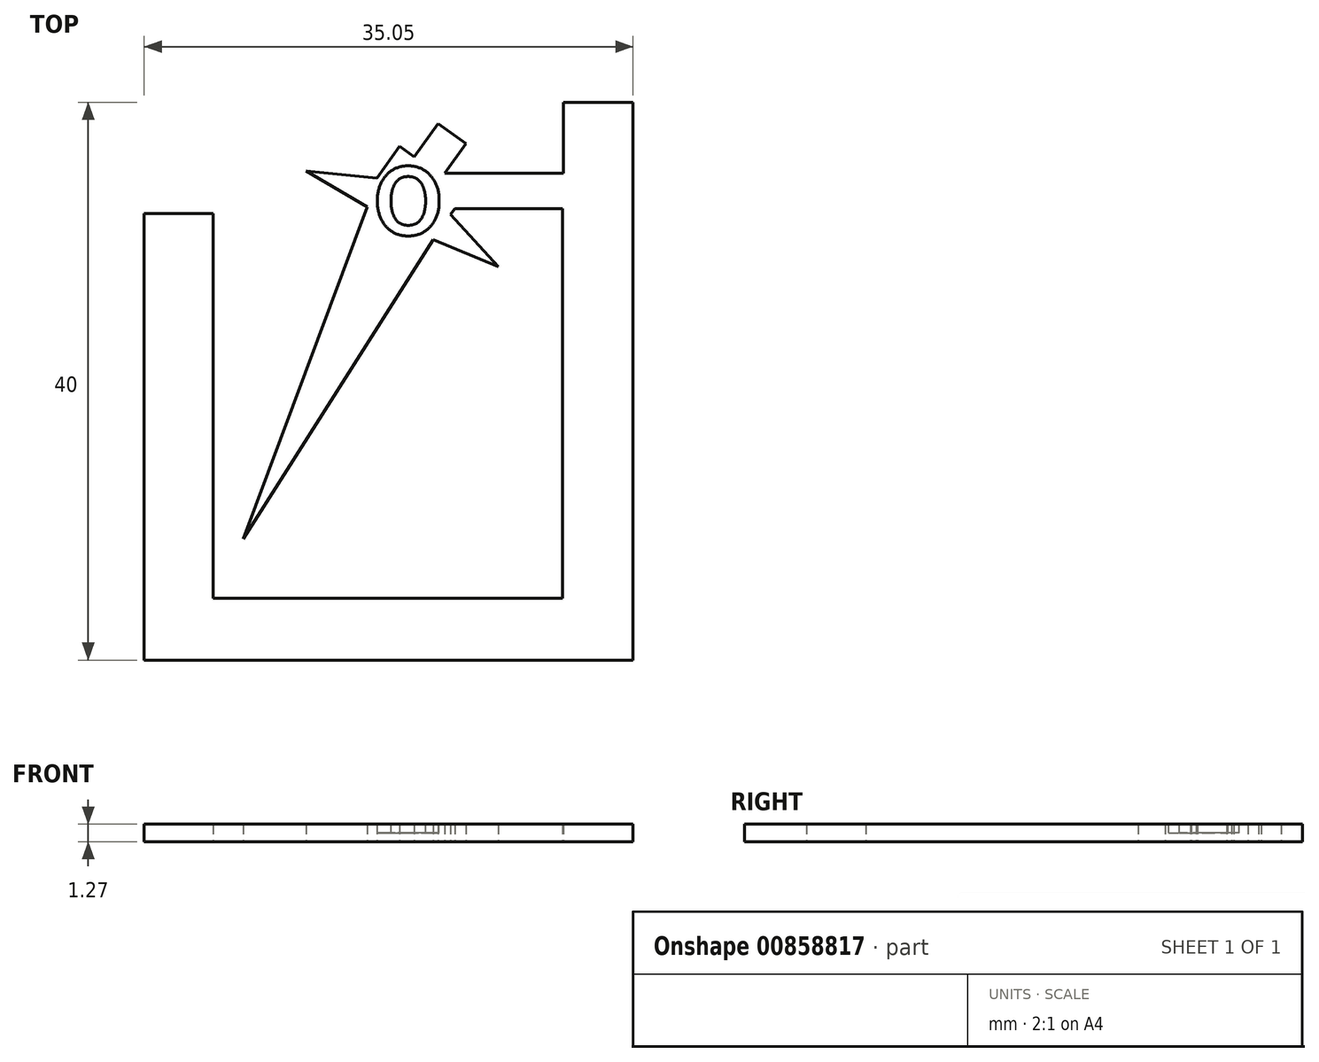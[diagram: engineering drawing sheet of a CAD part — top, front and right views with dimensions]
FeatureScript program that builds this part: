
annotation { "Feature Type Name" : "Feature", "Feature Type Description" : "" }
export const myFeature = defineFeature(function(context is Context, id is Id, definition is map)
    precondition{}
    {
        {
            var Q0;
            Q0=qCreatedBy(makeId("Top.planeOp"),FACE);
            var sketch = newSketch(context, id + "F0", { "sketchPlane" : qUnion([Q0])});
            skLineSegment(sketch, "E0.top", {"start": v(17.43, -24.7) * mm, "end": v(-17.62, -24.7) * mm});
            skLineSegment(sketch, "E0.left", {"start": v(17.43, 15.3) * mm, "end": v(17.43, -24.7) * mm});
            skLineSegment(sketch, "E1.top", {"start": v(12.4, -20.24) * mm, "end": v(-12.67, -20.24) * mm});
            skLineSegment(sketch, "E2", {"start": v(4.65, 7.7) * mm, "end": v(12.4, 7.7) * mm});
            skLineSegment(sketch, "E3", {"start": v(4.83, 9.22) * mm, "end": v(12.45, 9.22) * mm});
            skLineSegment(sketch, "E4", {"start": v(12.45, 15.3) * mm, "end": v(17.43, 15.3) * mm});
            skLineSegment(sketch, "E5", {"start": v(12.45, 9.22) * mm, "end": v(12.45, 15.3) * mm});
            skLineSegment(sketch, "E6", {"start": v(-17.62, 7.34) * mm, "end": v(-12.67, 7.34) * mm});
            skLineSegment(sketch, "E7", {"start": v(-17.62, 7.34) * mm, "end": v(-17.62, -24.7) * mm});
            skLineSegment(sketch, "E8", {"start": v(-12.67, 7.34) * mm, "end": v(-12.67, -20.24) * mm});
            skLineSegment(sketch, "E9", {"start": v(12.4, 7.7) * mm, "end": v(12.4, -20.24) * mm});
            skLineSegment(sketch, "E10", {"start": v(1.75, 11.42) * mm, "end": v(0.7, 12.17) * mm});
            skLineSegment(sketch, "E11", {"start": v(0.7, 12.17) * mm, "end": v(-0.93, 9.9) * mm});
            skLineSegment(sketch, "E12", {"start": v(3.95, 7.7) * mm, "end": v(3.74, 7.7) * mm});
            skLineSegment(sketch, "E13", {"start": v(-0.93, 9.9) * mm, "end": v(-5.99, 10.38) * mm});
            skLineSegment(sketch, "E14", {"start": v(-5.99, 10.38) * mm, "end": v(-1.61, 7.8) * mm});
            skLineSegment(sketch, "E15", {"start": v(-1.61, 7.8) * mm, "end": v(-10.5, -16) * mm});
            skLineSegment(sketch, "E16", {"start": v(12.45, 10.24) * mm, "end": v(3.95, 10.24) * mm});
            skPoint(sketch, "E17", {"position": v(2.76, 10.7) * mm});
            skLineSegment(sketch, "E18", {"start": v(-10.5, -16) * mm, "end": v(2.76, 10.7) * mm, "construction": true});
            skLineSegment(sketch, "E19.MirrorCS", {"start": v(7.8, 3.53) * mm, "end": v(3.1, 5.47) * mm});
            skLineSegment(sketch, "E20.MirrorCS", {"start": v(3.1, 5.47) * mm, "end": v(-10.5, -16) * mm});
            skLineSegment(sketch, "E21", {"start": v(7.8, 3.53) * mm, "end": v(4.35, 7.27) * mm});
            skPoint(sketch, "E22.MirrorCS.start.orphan", {"position": v(4.35, 7.27) * mm});
            skLineSegment(sketch, "E23", {"start": v(1.75, 11.42) * mm, "end": v(3.45, 13.79) * mm});
            skLineSegment(sketch, "E24", {"start": v(3.45, 13.79) * mm, "end": v(5.46, 12.36) * mm});
            skLineSegment(sketch, "E25", {"start": v(5.46, 12.36) * mm, "end": v(3.95, 10.24) * mm});
            skLineSegment(sketch, "E26", {"start": v(4.65, 7.7) * mm, "end": v(4.35, 7.27) * mm});
            skSolve(sketch);
        }
        {
            var Q0;
            Q0=makeQuery(id+"F0.imprint","IMPRINT",FACE,{"disambiguationData":[TD([[makeQuery(id+"F0.imprint","IMPRINT",EDGE,{"derivedFrom":sQuery(id+"F0.wireOp",EDGE,"E0.top")}),-1.0]])]});
            var Q1;
            {var subQ0=sQuery(id+"F0.wireOp",EDGE,"FKejiANf-u82S-7BPr-4an4-q4Ka4m4IZFMA");var subQ1=makeQuery(id+"F0.imprint","INTERSECT",VERTEX,{"derivedFrom":[sQuery(id+"F0.wireOp",EDGE,"1SfU6YIB-wvzm-6zBe-5eDS-HKFIA9QaUayn"),subQ0]});Q1=makeQuery(id+"F0.imprint","IMPRINT",FACE,{"disambiguationData":[TD([[makeQuery(id+"F0.imprint","IMPRINT",EDGE,{"disambiguationData":[TD([[subQ1,1.0]])],"derivedFrom":subQ0}),1.0]])]});}
            extrude(context, id + "F1", {"entities" : qUnion([Q0, Q1]), "depth" : 1.27 * mm, "offsetDistance" : 25.4 * mm});
        }
        {
            var Q0;
            Q0=makeQuery(id+"F1.opExtrude","CAP_FACE",FACE,{"disambiguationData":[OSD([sQuery(id+"F0.wireOp",EDGE,"E0.top"),sQuery(id+"F0.wireOp",EDGE,"E0.left"),sQuery(id+"F0.wireOp",EDGE,"E0.right"),sQuery(id+"F0.wireOp",EDGE,"E1.top"),sQuery(id+"F0.wireOp",EDGE,"E1.right"),sQuery(id+"F0.wireOp",EDGE,"1SfU6YIB-wvzm-6zBe-5eDS-HKFIA9QaUayn"),sQuery(id+"F0.wireOp",EDGE,"sM1Sgktc-x2VY-oS3Z-5OfG-QNgHwikTJDgL"),sQuery(id+"F0.wireOp",EDGE,"7EqO3XEm-McEN-PWzp-HPdO-5mDO97qVc4eW"),sQuery(id+"F0.wireOp",EDGE,"BdKeHqo0-FdcT-Rb85-6iZA-lVtgPkFKthWV"),sQuery(id+"F0.wireOp",EDGE,"FKejiANf-u82S-7BPr-4an4-q4Ka4m4IZFMA"),sQuery(id+"F0.wireOp",EDGE,"eK1Uujpq-Df3w-NQqX-Gc2k-lf4LO3mh3muX"),sQuery(id+"F0.wireOp",EDGE,"9dokPukG-NNzw-ETl1-5EZM-OfzmBowc8QZ2"),sQuery(id+"F0.wireOp",EDGE,"89ef536c-63d7-428c-8d95-022694007808.trimOffspring"),sQuery(id+"F0.wireOp",EDGE,"e37d3fe4-c149-4dc4-956f-d1983d31f44f.trimOffspring"),sQuery(id+"F0.wireOp",EDGE,"0ee4a390-7657-49db-9c73-643e63165271.trimOffspring"),sQuery(id+"F0.wireOp",EDGE,"eCGh251j-4Mt1-Y2Ib-rAlh-B7rz0UIJvHUj"),sQuery(id+"F0.wireOp",EDGE,"bES6kjNz-8YLn-JcT7-Q6dz-SQKSX46rVPbr")])],"isStart":false});
            var sketch = newSketch(context, id + "F2", { "sketchPlane" : qUnion([Q0])});
            skText(sketch, "E27", { "text": "O", "fontName": "RobotoSlab-Bold.ttf"});
            skPoint(sketch, "E28", {"position": v(1.42, 8.28) * mm});
            const initialGuessF2  = {"E27": [-0.00112, 0.0058, 1, 0, 0.00495]};
            skSetInitialGuess(sketch, initialGuessF2);
            skSolve(sketch);
        }
        {
            var Q0;
            Q0=makeQuery(id+"F2.imprint","IMPRINT",FACE,{"disambiguationData":[TD([[makeQuery(id+"F2.imprint","IMPRINT",EDGE,{"derivedFrom":sQuery(id+"F2.wireOp",EDGE,"E27.sketch_text.stroke-16")}),-1.0]])]});
            var Q1;
            Q1=makeQuery(id+"F2.imprint","IMPRINT",FACE,{"disambiguationData":[TD([[makeQuery(id+"F2.imprint","IMPRINT",EDGE,{"derivedFrom":sQuery(id+"F2.wireOp",EDGE,"E27.sketch_text.stroke-0")}),-1.0]])]});
            extrude(context, id + "F3", {"entities" : qUnion([Q0, Q1]), "operationType" : NewBodyOperationType.REMOVE, "oppositeDirection" : true, "depth" : 0.64 * mm, "offsetDistance" : 25.4 * mm});
        }
    });
